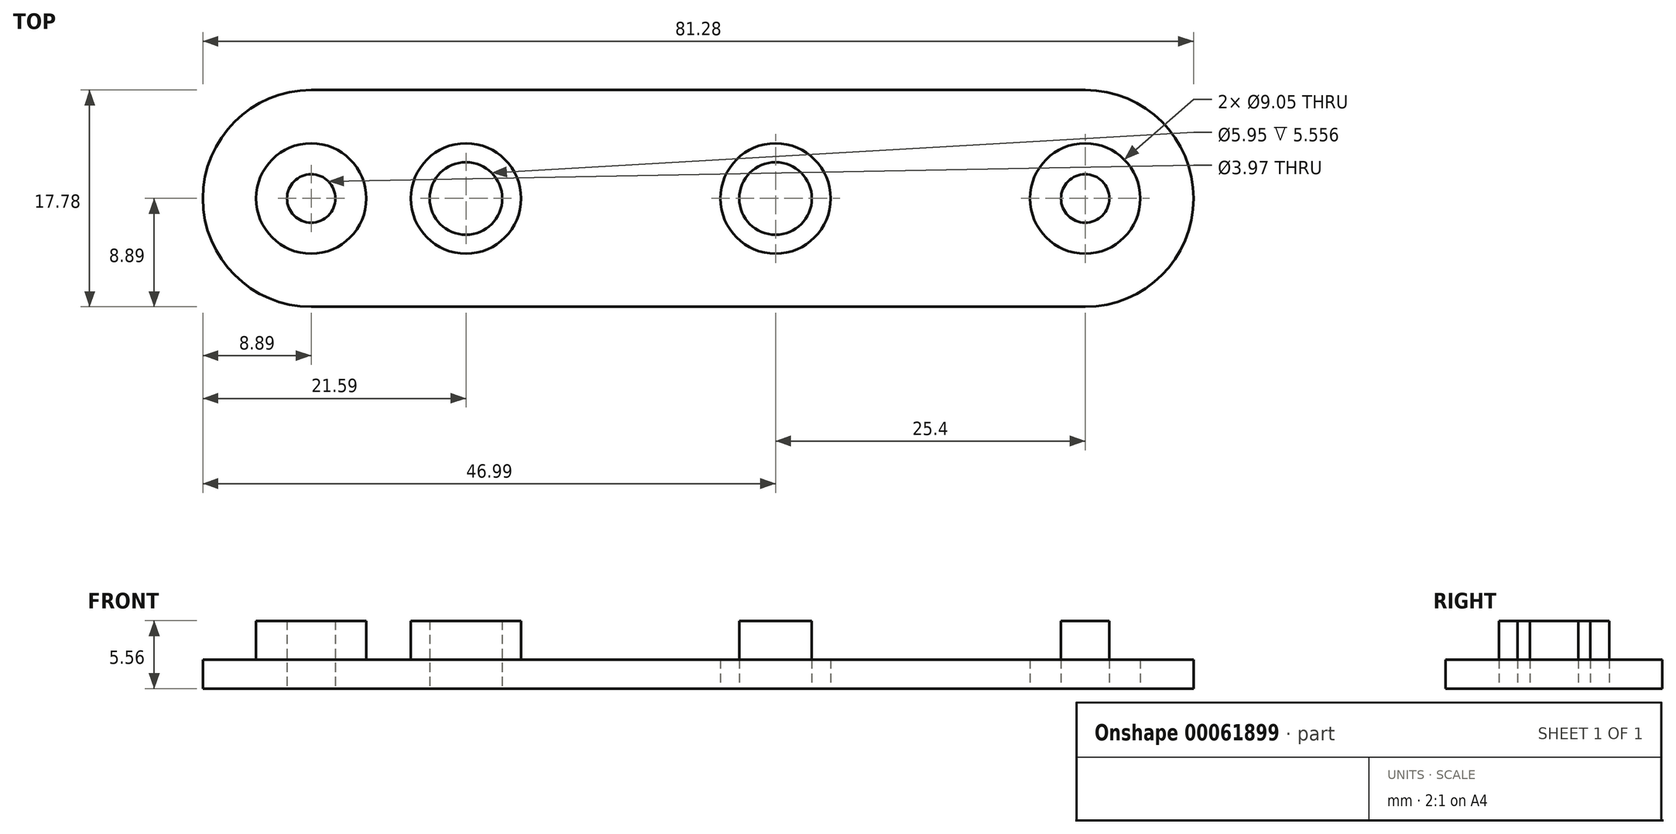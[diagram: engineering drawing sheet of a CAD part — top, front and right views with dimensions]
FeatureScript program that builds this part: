
annotation { "Feature Type Name" : "Feature", "Feature Type Description" : "" }
export const myFeature = defineFeature(function(context is Context, id is Id, definition is map)
    precondition{}
    {
        {
            var Q0;
            Q0=qCreatedBy(makeId("Top.planeOp"),FACE);
            var sketch = newSketch(context, id + "F0", { "sketchPlane" : qUnion([Q0])});
            skCircle(sketch, "E0", {"center": v(-6.35, 0) * mm, "radius": 2.98 * mm});
            skCircle(sketch, "E1", {"center": v(-19.05, 0) * mm, "radius": 1.98 * mm});
            skLineSegment(sketch, "E2", {"start": v(0, 11.31) * mm, "end": v(0, -14.48) * mm, "construction": true});
            skCircle(sketch, "E3.MirrorC", {"center": v(44.45, 0) * mm, "radius": 1.98 * mm});
            skCircle(sketch, "E4.MirrorC", {"center": v(19.05, 0) * mm, "radius": 2.98 * mm});
            skCircle(sketch, "E5.0", {"center": v(-19.05, 0) * mm, "radius": 4.52 * mm});
            skCircle(sketch, "E6", {"center": v(-6.35, 0) * mm, "radius": 4.52 * mm});
            skCircle(sketch, "E7", {"center": v(19.05, 0) * mm, "radius": 4.52 * mm});
            skCircle(sketch, "E8", {"center": v(44.45, 0) * mm, "radius": 4.52 * mm});
            skArc(sketch, "E9", {"start": v(-19.05, -8.9) * mm, "mid": v(-27.94, 0) * mm, "end": v(-19.05, 8.9) * mm});
            skArc(sketch, "E10", {"start": v(44.45, 8.9) * mm, "mid": v(53.34, 0) * mm, "end": v(44.45, -8.9) * mm});
            skLineSegment(sketch, "E11", {"start": v(-19.05, 8.9) * mm, "end": v(44.45, 8.9) * mm});
            skLineSegment(sketch, "E12", {"start": v(-19.05, -8.9) * mm, "end": v(44.45, -8.9) * mm});
            skSolve(sketch);
        }
        {
            var Q0;
            Q0=makeQuery(id+"F0.imprint","IMPRINT",FACE,{"disambiguationData":[TD([[makeQuery(id+"F0.imprint","IMPRINT",EDGE,{"derivedFrom":sQuery(id+"F0.wireOp",EDGE,"E5.0")}),-1.0]])]});
            extrude(context, id + "F1", {"entities" : qUnion([Q0]), "depth" : 2.38 * mm});
        }
        {
            var Q0;
            Q0=makeQuery(id+"F0.imprint","IMPRINT",FACE,{"disambiguationData":[TD([[makeQuery(id+"F0.imprint","IMPRINT",EDGE,{"derivedFrom":sQuery(id+"F0.wireOp",EDGE,"E1")}),-1.0]])]});
            var Q1;
            Q1=makeQuery(id+"F0.imprint","IMPRINT",FACE,{"disambiguationData":[TD([[makeQuery(id+"F0.imprint","IMPRINT",EDGE,{"derivedFrom":sQuery(id+"F0.wireOp",EDGE,"E0")}),-1.0]])]});
            var Q2;
            Q2=makeQuery(id+"F0.imprint","IMPRINT",FACE,{"disambiguationData":[TD([[makeQuery(id+"F0.imprint","IMPRINT",EDGE,{"derivedFrom":sQuery(id+"F0.wireOp",EDGE,"E4.MirrorC")}),1.0]])]});
            var Q3;
            Q3=makeQuery(id+"F0.imprint","IMPRINT",FACE,{"disambiguationData":[TD([[makeQuery(id+"F0.imprint","IMPRINT",EDGE,{"derivedFrom":sQuery(id+"F0.wireOp",EDGE,"E3.MirrorC")}),1.0]])]});
            extrude(context, id + "F2", {"entities" : qUnion([Q0, Q1, Q2, Q3]), "operationType" : NewBodyOperationType.ADD, "depth" : 5.56 * mm});
        }
    });
